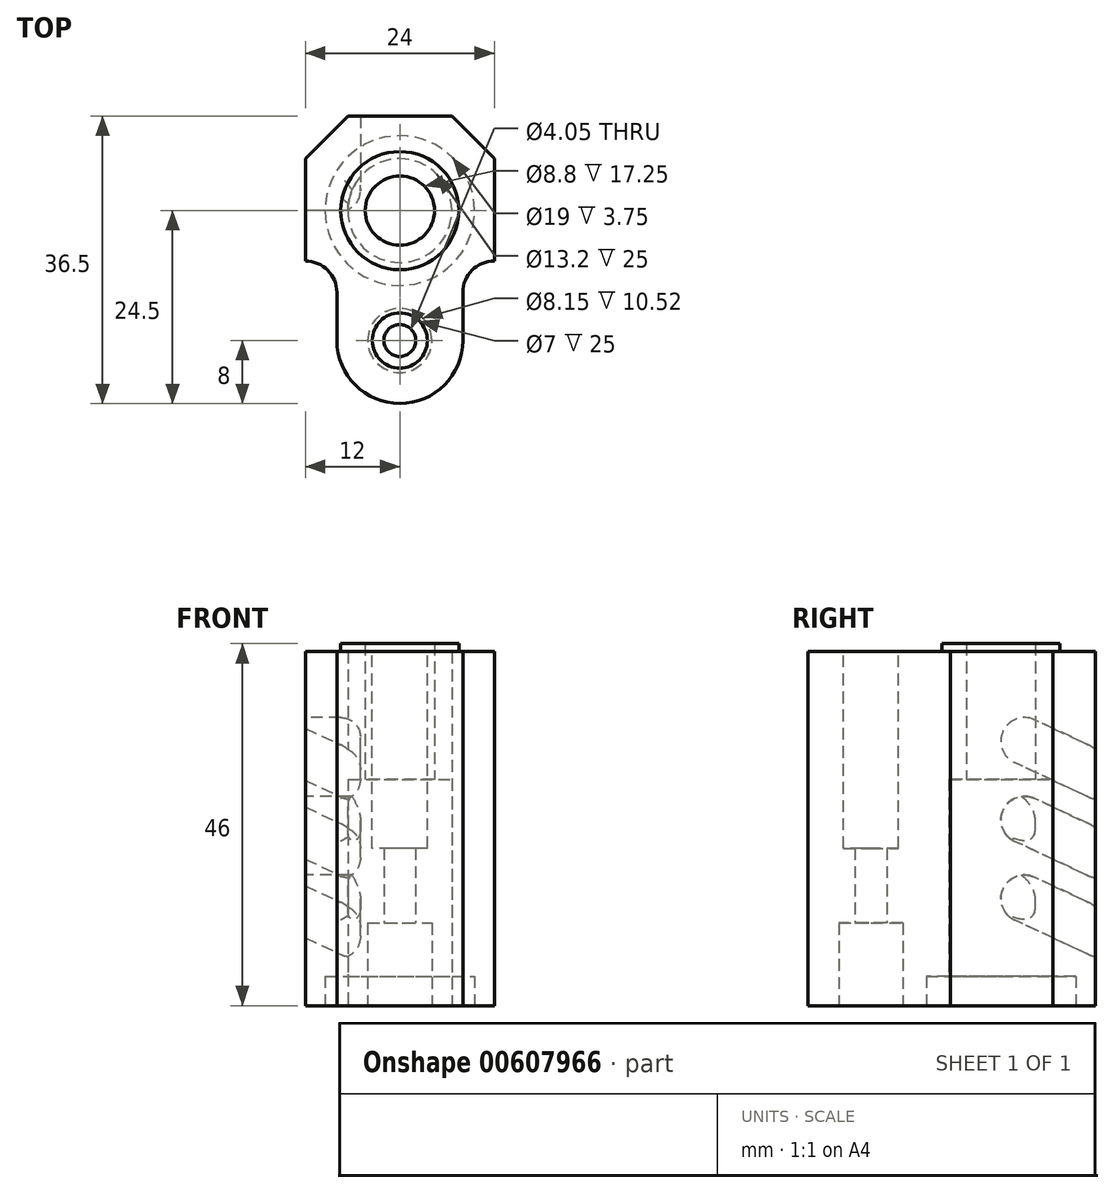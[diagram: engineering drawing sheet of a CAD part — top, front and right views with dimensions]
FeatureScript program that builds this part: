
annotation { "Feature Type Name" : "Feature", "Feature Type Description" : "" }
export const myFeature = defineFeature(function(context is Context, id is Id, definition is map)
    precondition{}
    {
        {
            var Q0;
            Q0=qCreatedBy(makeId("Top.planeOp"),FACE);
            var sketch = newSketch(context, id + "F0", { "sketchPlane" : qUnion([Q0])});
            skCircle(sketch, "E0", {"center": v(0, 0) * mm, "radius": 4.4 * mm});
            skLineSegment(sketch, "E1", {"start": v(0, 12) * mm, "end": v(-6.6, 12) * mm});
            skLineSegment(sketch, "E2", {"start": v(-6.6, 12) * mm, "end": v(-12, 6.6) * mm});
            skLineSegment(sketch, "E3", {"start": v(-12, 6.6) * mm, "end": v(-12, -6.4) * mm});
            skArc(sketch, "E4", {"start": v(-8, -10.4) * mm, "mid": v(-9.17, -7.57) * mm, "end": v(-12, -6.4) * mm});
            skLineSegment(sketch, "E5", {"start": v(-8, -10.4) * mm, "end": v(-8, -16.5) * mm});
            skArc(sketch, "E6", {"start": v(-8, -16.5) * mm, "mid": v(0, -24.5) * mm, "end": v(8, -16.5) * mm});
            skLineSegment(sketch, "E7.MirrorCS", {"start": v(8, -10.4) * mm, "end": v(8, -16.5) * mm});
            skArc(sketch, "E8.MirrorCS", {"start": v(8, -10.4) * mm, "mid": v(9.17, -7.57) * mm, "end": v(12, -6.4) * mm});
            skLineSegment(sketch, "E9.MirrorCS", {"start": v(12, 6.6) * mm, "end": v(12, -6.4) * mm});
            skLineSegment(sketch, "E10.MirrorCS", {"start": v(6.6, 12) * mm, "end": v(12, 6.6) * mm});
            skLineSegment(sketch, "E11.MirrorCS", {"start": v(0, 12) * mm, "end": v(6.6, 12) * mm});
            skCircle(sketch, "E12", {"center": v(0, -16.5) * mm, "radius": 2.02 * mm});
            skSolve(sketch);
        }
        {
            var Q0;
            Q0=makeQuery(id+"F0.imprint","IMPRINT",FACE,{"disambiguationData":[TD([[makeQuery(id+"F0.imprint","IMPRINT",EDGE,{"derivedFrom":sQuery(id+"F0.wireOp",EDGE,"E0")}),-1.0]])]});
            extrude(context, id + "F1", {"entities" : qUnion([Q0]), "depth" : 45 * mm, "offsetDistance" : 25 * mm});
        }
        {
            var Q0;
            Q0=makeQuery(id+"F1.opExtrude","CAP_FACE",FACE,{"disambiguationData":[OSD([sQuery(id+"F0.wireOp",EDGE,"E0"),sQuery(id+"F0.wireOp",EDGE,"E1"),sQuery(id+"F0.wireOp",EDGE,"E2"),sQuery(id+"F0.wireOp",EDGE,"E3"),sQuery(id+"F0.wireOp",EDGE,"E4"),sQuery(id+"F0.wireOp",EDGE,"E5"),sQuery(id+"F0.wireOp",EDGE,"E6"),sQuery(id+"F0.wireOp",EDGE,"E7.MirrorCS"),sQuery(id+"F0.wireOp",EDGE,"E8.MirrorCS"),sQuery(id+"F0.wireOp",EDGE,"E9.MirrorCS"),sQuery(id+"F0.wireOp",EDGE,"E10.MirrorCS"),sQuery(id+"F0.wireOp",EDGE,"E11.MirrorCS"),sQuery(id+"F0.wireOp",EDGE,"E12")])],"isStart":true});
            var sketch = newSketch(context, id + "F2", { "sketchPlane" : qUnion([Q0])});
            skCircle(sketch, "E13", {"center": v(0, 0) * mm, "radius": 9.5 * mm});
            skSolve(sketch);
        }
        {
            var Q0;
            Q0=makeQuery(id+"F2.imprint","IMPRINT",FACE,{"disambiguationData":[TD([[makeQuery(id+"F2.imprint","IMPRINT",EDGE,{"derivedFrom":sQuery(id+"F2.wireOp",EDGE,"E13")}),1.0]])]});
            extrude(context, id + "F3", {"entities" : qUnion([Q0]), "operationType" : NewBodyOperationType.REMOVE, "oppositeDirection" : true, "depth" : 3.75 * mm, "offsetDistance" : 25 * mm});
        }
        {
            var Q0;
            Q0=makeQuery(id+"F3.boolean.opBoolean","COPY",FACE,{"derivedFrom":makeQuery(id+"F3.opExtrude","CAP_FACE",FACE,{"disambiguationData":[OSD([sQuery(id+"F0.wireOp",EDGE,"E0"),sQuery(id+"F2.wireOp",EDGE,"E13")])],"isStart":false})});
            var sketch = newSketch(context, id + "F4", { "sketchPlane" : qUnion([Q0])});
            skCircle(sketch, "E14", {"center": v(0, 0) * mm, "radius": 6.6 * mm});
            skSolve(sketch);
        }
        {
            var Q0;
            Q0=makeQuery(id+"F4.imprint","IMPRINT",FACE,{"disambiguationData":[TD([[makeQuery(id+"F4.imprint","IMPRINT",EDGE,{"derivedFrom":sQuery(id+"F4.wireOp",EDGE,"E14")}),1.0]])]});
            extrude(context, id + "F5", {"entities" : qUnion([Q0]), "operationType" : NewBodyOperationType.REMOVE, "oppositeDirection" : true, "depth" : 25 * mm, "offsetDistance" : 25 * mm});
        }
        {
            var Q0;
            Q0=makeQuery(id+"F1.opExtrude","CAP_FACE",FACE,{"disambiguationData":[OSD([sQuery(id+"F0.wireOp",EDGE,"E0"),sQuery(id+"F0.wireOp",EDGE,"E1"),sQuery(id+"F0.wireOp",EDGE,"E2"),sQuery(id+"F0.wireOp",EDGE,"E3"),sQuery(id+"F0.wireOp",EDGE,"E4"),sQuery(id+"F0.wireOp",EDGE,"E5"),sQuery(id+"F0.wireOp",EDGE,"E6"),sQuery(id+"F0.wireOp",EDGE,"E7.MirrorCS"),sQuery(id+"F0.wireOp",EDGE,"E8.MirrorCS"),sQuery(id+"F0.wireOp",EDGE,"E9.MirrorCS"),sQuery(id+"F0.wireOp",EDGE,"E10.MirrorCS"),sQuery(id+"F0.wireOp",EDGE,"E11.MirrorCS"),sQuery(id+"F0.wireOp",EDGE,"E12")])],"isStart":true});
            var sketch = newSketch(context, id + "F6", { "sketchPlane" : qUnion([Q0])});
            skCircle(sketch, "E15", {"center": v(0, 16.5) * mm, "radius": 3 * mm});
            skSolve(sketch);
        }
        {
            var Q0;
            Q0=makeQuery(id+"F6.imprint","IMPRINT",FACE,{"disambiguationData":[TD([[makeQuery(id+"F6.imprint","IMPRINT",EDGE,{"derivedFrom":sQuery(id+"F6.wireOp",EDGE,"E15")}),1.0]])]});
            extrude(context, id + "F7", {"entities" : qUnion([Q0]), "operationType" : NewBodyOperationType.REMOVE, "oppositeDirection" : true, "depth" : 10 * mm, "offsetDistance" : 25 * mm});
        }
        {
            var Q0;
            Q0=makeQuery(id+"F1.opExtrude","CAP_FACE",FACE,{"disambiguationData":[OSD([sQuery(id+"F0.wireOp",EDGE,"E0"),sQuery(id+"F0.wireOp",EDGE,"E1"),sQuery(id+"F0.wireOp",EDGE,"E2"),sQuery(id+"F0.wireOp",EDGE,"E3"),sQuery(id+"F0.wireOp",EDGE,"E4"),sQuery(id+"F0.wireOp",EDGE,"E5"),sQuery(id+"F0.wireOp",EDGE,"E6"),sQuery(id+"F0.wireOp",EDGE,"E7.MirrorCS"),sQuery(id+"F0.wireOp",EDGE,"E8.MirrorCS"),sQuery(id+"F0.wireOp",EDGE,"E9.MirrorCS"),sQuery(id+"F0.wireOp",EDGE,"E10.MirrorCS"),sQuery(id+"F0.wireOp",EDGE,"E11.MirrorCS"),sQuery(id+"F0.wireOp",EDGE,"E12")])],"isStart":true});
            var sketch = newSketch(context, id + "F8", { "sketchPlane" : qUnion([Q0])});
            skCircle(sketch, "E16", {"center": v(0, 16.5) * mm, "radius": 4.08 * mm});
            skSolve(sketch);
        }
        {
            var Q0;
            Q0 = qSketchRegion(id + "F8", true);
            extrude(context, id + "F9", {"entities" : qUnion([Q0]), "operationType" : NewBodyOperationType.REMOVE, "flatOperationType" : FlatOperationType.REMOVE, "oppositeDirection" : true, "depth" : 10.52 * mm, "offsetDistance" : 25 * mm, "domain" : OperationDomain.MODEL});
        }
        {
            var Q0;
            Q0=makeQuery(id+"F1.opExtrude","CAP_FACE",FACE,{"disambiguationData":[OSD([sQuery(id+"F0.wireOp",EDGE,"E0"),sQuery(id+"F0.wireOp",EDGE,"E1"),sQuery(id+"F0.wireOp",EDGE,"E2"),sQuery(id+"F0.wireOp",EDGE,"E3"),sQuery(id+"F0.wireOp",EDGE,"E4"),sQuery(id+"F0.wireOp",EDGE,"E5"),sQuery(id+"F0.wireOp",EDGE,"E6"),sQuery(id+"F0.wireOp",EDGE,"E7.MirrorCS"),sQuery(id+"F0.wireOp",EDGE,"E8.MirrorCS"),sQuery(id+"F0.wireOp",EDGE,"E9.MirrorCS"),sQuery(id+"F0.wireOp",EDGE,"E10.MirrorCS"),sQuery(id+"F0.wireOp",EDGE,"E11.MirrorCS"),sQuery(id+"F0.wireOp",EDGE,"E12")])],"isStart":false});
            var sketch = newSketch(context, id + "F10", { "sketchPlane" : qUnion([Q0])});
            skCircle(sketch, "E17", {"center": v(0, -16.5) * mm, "radius": 3.5 * mm});
            skSolve(sketch);
        }
        {
            var Q0;
            Q0 = qSketchRegion(id + "F10", true);
            extrude(context, id + "F11", {"entities" : qUnion([Q0]), "operationType" : NewBodyOperationType.REMOVE, "oppositeDirection" : true, "depth" : 25 * mm, "offsetDistance" : 25 * mm});
        }
        {
            var Q0;
            Q0=makeQuery(id+"F1.opExtrude","SWEPT_FACE",FACE,{"disambiguationData":[OSD([sQuery(id+"F0.wireOp",EDGE,"E3")])]});
            var sketch = newSketch(context, id + "F12", { "sketchPlane" : qUnion([Q0])});
            skSolve(sketch);
        }
        {
            var Q0;
            {var subQ0=sQuery(id+"F0.wireOp",EDGE,"E3");Q0=makeQuery(id+"F12.imprint","IMPRINT",FACE,{"disambiguationData":[TD([[makeQuery(id+"F12.imprint","IMPRINT",EDGE,{"derivedFrom":makeQuery(id+"F1.opExtrude","CAP_EDGE",EDGE,{"disambiguationData":[OSD([subQ0])],"isStart":true})}),1.0]])]});}
            var sketch = newSketch(context, id + "F13", { "sketchPlane" : qUnion([Q0])});
            skLineSegment(sketch, "E18", {"start": v(0, 15) * mm, "end": v(-15.53, 7.76) * mm, "construction": true});
            skArc(sketch, "E19", {"start": v(-1.73, 10.88) * mm, "mid": v(-0.28, 14.87) * mm, "end": v(-4.27, 16.32) * mm});
            skLineSegment(sketch, "E20", {"start": v(0, 0) * mm, "end": v(0, 32.79) * mm, "construction": true});
            skArc(sketch, "E21", {"start": v(-16.8, 10.48) * mm, "mid": v(-18.25, 6.49) * mm, "end": v(-14.26, 5.04) * mm});
            skLineSegment(sketch, "E22", {"start": v(-16.8, 10.48) * mm, "end": v(-4.27, 16.32) * mm});
            skLineSegment(sketch, "E23", {"start": v(-14.26, 5.04) * mm, "end": v(-1.73, 10.88) * mm});
            skLineSegment(sketch, "E24.direction1", {"start": v(0, 0) * mm, "end": v(25, 0) * mm, "construction": true});
            skLineSegment(sketch, "E25.0.1.0", {"start": v(-14.26, 15.04) * mm, "end": v(-1.73, 20.88) * mm});
            skLineSegment(sketch, "E25.0.1.1", {"start": v(-16.8, 20.48) * mm, "end": v(-4.27, 26.32) * mm});
            skArc(sketch, "E25.0.1.2", {"start": v(-16.8, 20.48) * mm, "mid": v(-18.25, 16.49) * mm, "end": v(-14.26, 15.04) * mm});
            skArc(sketch, "E25.0.1.3", {"start": v(-1.73, 20.88) * mm, "mid": v(-0.28, 24.87) * mm, "end": v(-4.27, 26.32) * mm});
            skLineSegment(sketch, "E25.0.1.4", {"start": v(0, 25) * mm, "end": v(-15.53, 17.76) * mm, "construction": true});
            skLineSegment(sketch, "E25.0.2.0", {"start": v(-14.26, 25.04) * mm, "end": v(-1.73, 30.88) * mm});
            skLineSegment(sketch, "E25.0.2.1", {"start": v(-16.8, 30.48) * mm, "end": v(-4.27, 36.32) * mm});
            skArc(sketch, "E25.0.2.2", {"start": v(-16.8, 30.48) * mm, "mid": v(-18.25, 26.49) * mm, "end": v(-14.26, 25.04) * mm});
            skArc(sketch, "E25.0.2.3", {"start": v(-1.73, 30.88) * mm, "mid": v(-0.28, 34.87) * mm, "end": v(-4.27, 36.32) * mm});
            skLineSegment(sketch, "E25.0.2.4", {"start": v(0, 35) * mm, "end": v(-15.53, 27.76) * mm, "construction": true});
            skLineSegment(sketch, "E25.direction1", {"start": v(-16.8, 10.48) * mm, "end": v(-46.7, 10.48) * mm, "construction": true});
            skLineSegment(sketch, "E25.direction2", {"start": v(-16.8, 10.48) * mm, "end": v(-16.8, 20.48) * mm, "construction": true});
            skSolve(sketch);
        }
        {
            var Q0;
            Q0 = qSketchRegion(id + "F13", true);
            extrude(context, id + "F14", {"entities" : qUnion([Q0]), "operationType" : NewBodyOperationType.REMOVE, "oppositeDirection" : true, "depth" : 7 * mm, "offsetDistance" : 25 * mm});
        }
        {
            var Q0;
            Q0=makeQuery(id+"F14.boolean.opBoolean","COPY",EDGE,{"derivedFrom":makeQuery(id+"F14.opExtrude","CAP_EDGE",EDGE,{"disambiguationData":[OSD([sQuery(id+"F13.wireOp",EDGE,"E23")])],"isStart":false})});
            var Q1;
            Q1=makeQuery(id+"F14.boolean.opBoolean","COPY",EDGE,{"derivedFrom":makeQuery(id+"F14.opExtrude","CAP_EDGE",EDGE,{"disambiguationData":[OSD([sQuery(id+"F13.wireOp",EDGE,"E22")])],"isStart":false})});
            var Q2;
            Q2=makeQuery(id+"F14.boolean.opBoolean","COPY",EDGE,{"derivedFrom":makeQuery(id+"F14.opExtrude","CAP_EDGE",EDGE,{"disambiguationData":[OSD([sQuery(id+"F13.wireOp",EDGE,"E25.0.1.0")])],"isStart":false})});
            var Q3;
            Q3=makeQuery(id+"F14.boolean.opBoolean","COPY",EDGE,{"derivedFrom":makeQuery(id+"F14.opExtrude","CAP_EDGE",EDGE,{"disambiguationData":[OSD([sQuery(id+"F13.wireOp",EDGE,"E25.0.1.1")])],"isStart":false})});
            var Q4;
            Q4=makeQuery(id+"F14.boolean.opBoolean","COPY",EDGE,{"derivedFrom":makeQuery(id+"F14.opExtrude","CAP_EDGE",EDGE,{"disambiguationData":[OSD([sQuery(id+"F13.wireOp",EDGE,"E25.0.2.0")])],"isStart":false})});
            var Q5;
            Q5=makeQuery(id+"F6be6rTm9QDvujG_1.1.F14.boolean.opBoolean","COPY",EDGE,{"derivedFrom":makeQuery(id+"F6be6rTm9QDvujG_1.1.F14.opExtrude","CAP_EDGE",EDGE,{"disambiguationData":[OSD([sQuery(id+"F13.wireOp",EDGE,"E25.0.2.0")])],"isStart":false})});
            var Q6;
            Q6=makeQuery(id+"F6be6rTm9QDvujG_1.1.F14.boolean.opBoolean","COPY",EDGE,{"derivedFrom":makeQuery(id+"F6be6rTm9QDvujG_1.1.F14.opExtrude","CAP_EDGE",EDGE,{"disambiguationData":[OSD([sQuery(id+"F13.wireOp",EDGE,"E25.0.1.0")])],"isStart":false})});
            var Q7;
            Q7=makeQuery(id+"F6be6rTm9QDvujG_1.1.F14.boolean.opBoolean","COPY",EDGE,{"derivedFrom":makeQuery(id+"F6be6rTm9QDvujG_1.1.F14.opExtrude","CAP_EDGE",EDGE,{"disambiguationData":[OSD([sQuery(id+"F13.wireOp",EDGE,"E25.0.1.1")])],"isStart":false})});
            var Q8;
            Q8=makeQuery(id+"F6be6rTm9QDvujG_1.1.F14.boolean.opBoolean","COPY",EDGE,{"derivedFrom":makeQuery(id+"F6be6rTm9QDvujG_1.1.F14.opExtrude","CAP_EDGE",EDGE,{"disambiguationData":[OSD([sQuery(id+"F13.wireOp",EDGE,"E22")])],"isStart":false})});
            var Q9;
            Q9=makeQuery(id+"F6be6rTm9QDvujG_1.1.F14.boolean.opBoolean","COPY",EDGE,{"derivedFrom":makeQuery(id+"F6be6rTm9QDvujG_1.1.F14.opExtrude","CAP_EDGE",EDGE,{"disambiguationData":[OSD([sQuery(id+"F13.wireOp",EDGE,"E23")])],"isStart":false})});
            fillet(context, id + "F15", {"entities" : qUnion([Q0, Q1, Q2, Q3, Q4, Q5, Q6, Q7, Q8, Q9]), "radius" : 2.5 * mm, "tangentPropagation" : true, "allowEdgeOverflow" : false});
        }
        {
            var Q0;
            Q0=makeQuery(id+"F1.opExtrude","CAP_FACE",FACE,{"disambiguationData":[OSD([sQuery(id+"F0.wireOp",EDGE,"E0"),sQuery(id+"F0.wireOp",EDGE,"E1"),sQuery(id+"F0.wireOp",EDGE,"E2"),sQuery(id+"F0.wireOp",EDGE,"E3"),sQuery(id+"F0.wireOp",EDGE,"E4"),sQuery(id+"F0.wireOp",EDGE,"E5"),sQuery(id+"F0.wireOp",EDGE,"E6"),sQuery(id+"F0.wireOp",EDGE,"E7.MirrorCS"),sQuery(id+"F0.wireOp",EDGE,"E8.MirrorCS"),sQuery(id+"F0.wireOp",EDGE,"E9.MirrorCS"),sQuery(id+"F0.wireOp",EDGE,"E10.MirrorCS"),sQuery(id+"F0.wireOp",EDGE,"E11.MirrorCS"),sQuery(id+"F0.wireOp",EDGE,"E12")])],"isStart":false});
            var sketch = newSketch(context, id + "F16", { "sketchPlane" : qUnion([Q0])});
            skCircle(sketch, "E26", {"center": v(0, 0) * mm, "radius": 7.5 * mm});
            skSolve(sketch);
        }
        {
            var Q0;
            Q0=makeQuery(id+"F16.imprint","IMPRINT",FACE,{"disambiguationData":[TD([[makeQuery(id+"F16.imprint","IMPRINT",EDGE,{"derivedFrom":sQuery(id+"F16.wireOp",EDGE,"E26")}),1.0]])]});
            extrude(context, id + "F17", {"entities" : qUnion([Q0]), "operationType" : NewBodyOperationType.ADD, "depth" : 1 * mm, "offsetDistance" : 25 * mm});
        }
    });
